# Revit family: DA_Клапан_регулятор_расхода воздуха_VAV систем_РРДРП_привод Belimo LMV-D3-MOD_VEOX
name_source: partatom
category: Арматура воздуховодов
units: mm (PartAtom-declared; Revit-internal decimal feet)

## family parameters
Всегда вертикально = Да
На основе рабочей плоскости = Нет
Общий = Нет
При загрузке вырезать с полостями = Нет
Размер круглого соединителя = Использовать диаметр
Тип детали = Вставляется

## types (2) — shared parameters
ADSK_Владелец вида = РРДРП
ADSK_Единица измерения = шт
ADSK_Завод-изготовитель = VEOX
ADSK_Количество = 1
Flap visbility 1 = Да
Insulation = Rock wool
Insulation filter = Z
Metal plate = Galvanized steel
Mode = P
Seal = Plastic
ОБЩ_ДатаСемейства = 20230704

## per-type parameters (varying)
| type | ADSK_Наименование краткое | ADSK_Обозначение | Drive visibility | Drive visibility-Z | Insulation visibility | вылет шумоизол | изоляция выбор |
| с изоляцией |  | КРДВ-П | Нет | Да | Да | 75 мм | 1 |
| без изоляции | РРДРП | РРДРП | Да | Нет | Нет | 1 мм | 0 |

## geometry (parser evidence)
native form markers: Blend x2, Extrusion x1, Sweep x8
no freeform markers — native parametric forms only
